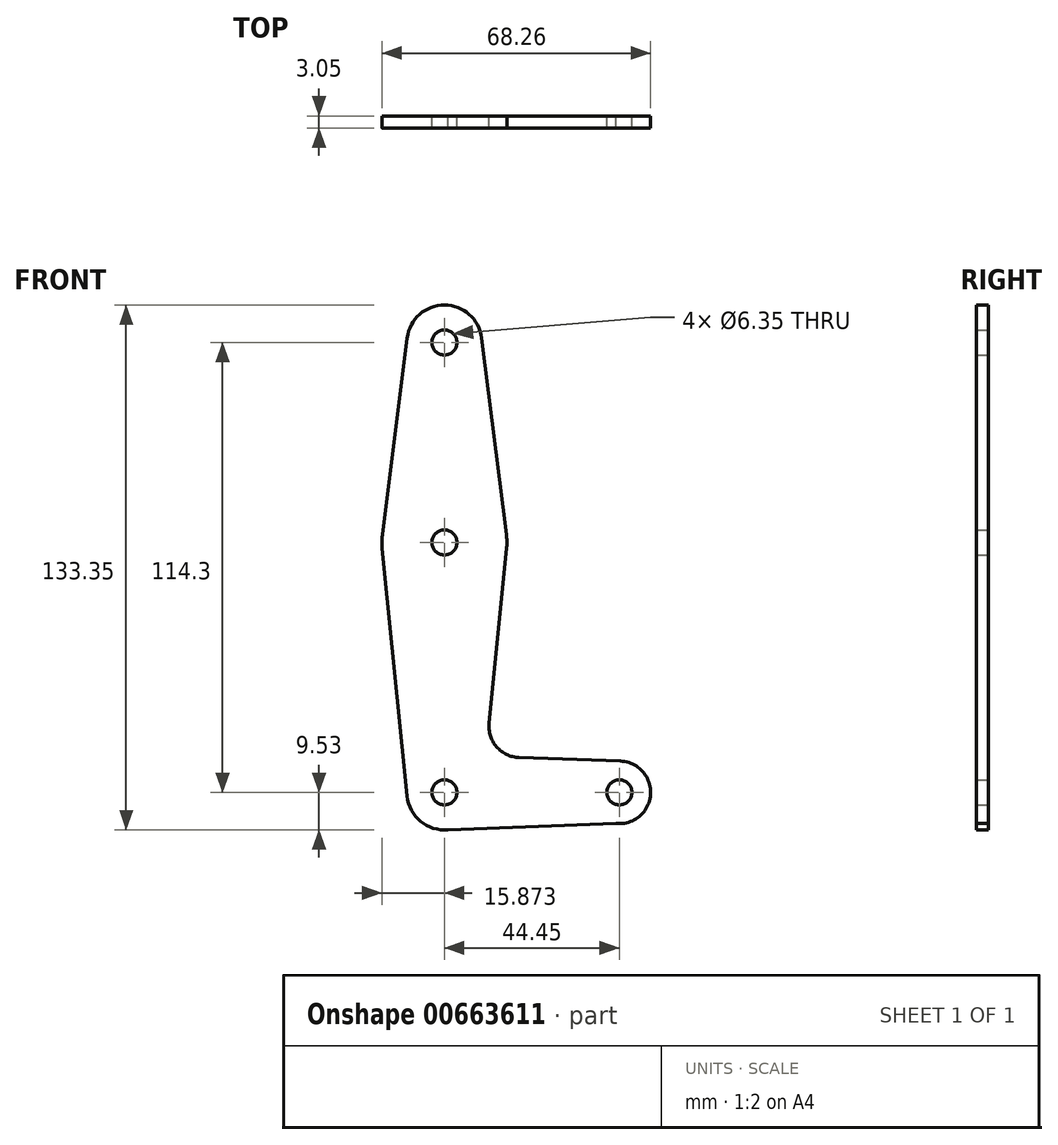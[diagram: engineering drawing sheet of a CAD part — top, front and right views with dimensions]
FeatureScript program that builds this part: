
annotation { "Feature Type Name" : "Feature", "Feature Type Description" : "" }
export const myFeature = defineFeature(function(context is Context, id is Id, definition is map)
    precondition{}
    {
        {
            var Q0;
            Q0=qCreatedBy(makeId("Front.planeOp"),FACE);
            var sketch = newSketch(context, id + "F0", { "sketchPlane" : qUnion([Q0])});
            skLineSegment(sketch, "E0", {"start": v(-31.25, 72.09) * mm, "end": v(-31.25, 68.91) * mm});
            skCircle(sketch, "E1", {"center": v(-31.25, 72.09) * mm, "radius": 9.53 * mm});
            skCircle(sketch, "E2", {"center": v(-31.25, 21.29) * mm, "radius": 15.88 * mm});
            skCircle(sketch, "E3", {"center": v(-31.25, -42.21) * mm, "radius": 9.53 * mm});
            skCircle(sketch, "E4", {"center": v(13.2, -42.21) * mm, "radius": 7.94 * mm});
            skLineSegment(sketch, "E5", {"start": v(-21.8, 73.28) * mm, "end": v(-15.5, 23.27) * mm});
            skLineSegment(sketch, "E6", {"start": v(-40.7, 73.28) * mm, "end": v(-47, 23.27) * mm});
            skLineSegment(sketch, "E7", {"start": v(-47.04, 19.7) * mm, "end": v(-40.72, -43.16) * mm});
            skLineSegment(sketch, "E8", {"start": v(-15.45, 19.7) * mm, "end": v(-19.9, -24.62) * mm});
            skLineSegment(sketch, "E9", {"start": v(-12.28, -33.36) * mm, "end": v(13.49, -34.28) * mm});
            skLineSegment(sketch, "E10", {"start": v(-30.32, -51.7) * mm, "end": v(14.63, -50.02) * mm});
            skArc(sketch, "E11.filletArc", {"start": v(-19.9, -24.62) * mm, "mid": v(-17.99, -30.64) * mm, "end": v(-12.28, -33.36) * mm});
            skCircle(sketch, "E12", {"center": v(-31.25, 21.29) * mm, "radius": 3.18 * mm});
            skCircle(sketch, "E13", {"center": v(-31.25, 72.09) * mm, "radius": 3.18 * mm});
            skCircle(sketch, "E14", {"center": v(-31.25, -42.21) * mm, "radius": 3.18 * mm});
            skCircle(sketch, "E15", {"center": v(13.2, -42.21) * mm, "radius": 3.18 * mm});
            skSolve(sketch);
        }
        {
            var Q0;
            Q0 = qSketchRegion(id + "F0", true);
            extrude(context, id + "F1", {"entities" : qUnion([Q0]), "depth" : 3.05 * mm, "offsetDistance" : 25.4 * mm});
        }
    });
